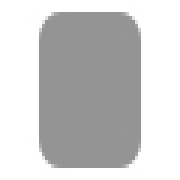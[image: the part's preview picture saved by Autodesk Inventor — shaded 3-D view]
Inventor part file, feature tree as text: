
AUTODESK INVENTOR PART (.ipt)
format: ipt  version: 2023.1 (Build 271208000, 208)  size: 103,424 bytes
history: native  units: in
note: dims shown in document units (in); Inventor stores cm internally (conversion verified against a paired STEP export)
features: extrude x1, fillet x1, chamfer x1, sketch x1
ambient origin geometry x8: Origin, YZ Plane, XZ Plane, XY Plane, X Axis, Y Axis, Z Axis, Center Point
bodies: Solid1 (feature_tree)
feature tree (4):
  extrude  "Extrusion1"  Depth=0.125in
  fillet  "Fillet1"  Radius=1.0in
  chamfer  "Chamfer1"  Distance=2.0in
  sketch  "Sketch1"  dims[d0=2.0in d1=1.0in d2=1.0in d3=2.0in d4=0.125in d5=0.0in d6=0.0in d7=0.0in d8=0.0in d9=0.125in d10=45.0deg d11=0.0in]
